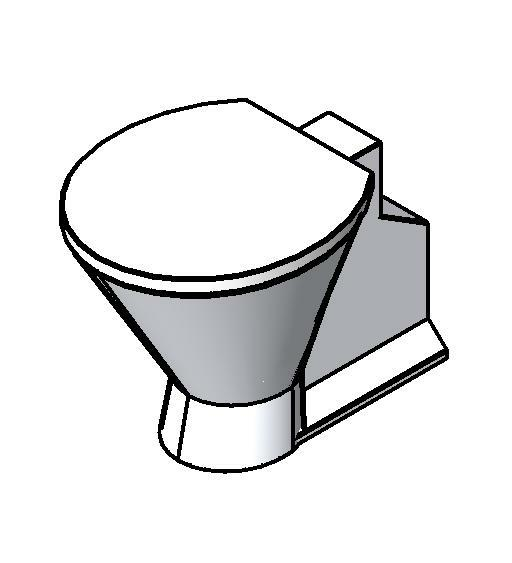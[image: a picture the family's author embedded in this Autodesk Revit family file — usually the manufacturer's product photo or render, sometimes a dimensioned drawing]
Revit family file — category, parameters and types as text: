
# Revit family: 23799-Deca_Torneira de Bancada Bica Alta_Pérola_1191-108
name_source: partatom
category: Plumbing Fixtures
units: mm (PartAtom-declared; Revit-internal decimal feet)

## family parameters
Cut with Voids When Loaded = No
Host = Face
Part Type = Normal
Room Calculation Point = No
Round Connector Dimension = Use Radius
Shared = No

## types (2) — shared parameters
Acompanha o Produto = BASE LATERAL COM MECANISMO,CHAVE DO AREJADOR,CHAVE ALLEN
Aprovado por = quattroD
Atendimento ao Cliente = 0800 011 7073
Categoria = METAIS PARA BANHEIRO
Composição Anel Vedação = -
Composição Assento = -
Composição Básica = Liga de Cobre (bronze e latão),Plásticos de Engenharia,Elastômeros
Composição Componente = -
Consumo = -
Cor Interna = -
Cor Secundária = -
Cores Componente = -
Criado por = quattroD
Código Pai = 1191.C108.MT
Diâmetro Água Fria = 0.02 m
Informações Complementares = -
Itens de Instalação = CHAVE ALLEN
Linha = Pérola
Manufacturer = Deca
Norma = NBR 10281
Peso Líquido (Kg) = 0.944
Pressão mín. Aquec. Acúmulo = -
Pressão mín. Aquec. Passagem = -
Raio Água Fria = 0.01 m
Saída de Esgoto = -
Segmento = -
Tipo de dispositivo economizador = DECA COMFORT
Tipo de mecanismo utilizado = MVC  - 1/4 de volta
Tipo de rosca de entrada = BSP NBR 8133
Tipo de rosca de saída = -
URL = www.deca.com.br
zero-valued in all types: CWFU, Default Elevation, Diâmetro Ponto de Esgoto, Raio Ponto de Esgoto, WFU

## per-type parameters (varying)
| type | Cor Principal | Description | Material | Model |
| 1191.C108.MT_CROMADO | Cromado Matte | TORN LAV MESA B ALTA DN15 PEROLA-CR | Deca_Cromado | 1191.C108.MT |
| 1191.SM108.MT_SUMMER GOLD | Summer Gold | TORN LAV MESA B ALTA DN15 PEROLA-SM MT | Deca_Summer Gold | 1191.SM108.MT |

## geometry (parser evidence)
native form markers: Sweep x2
no freeform markers — native parametric forms only
